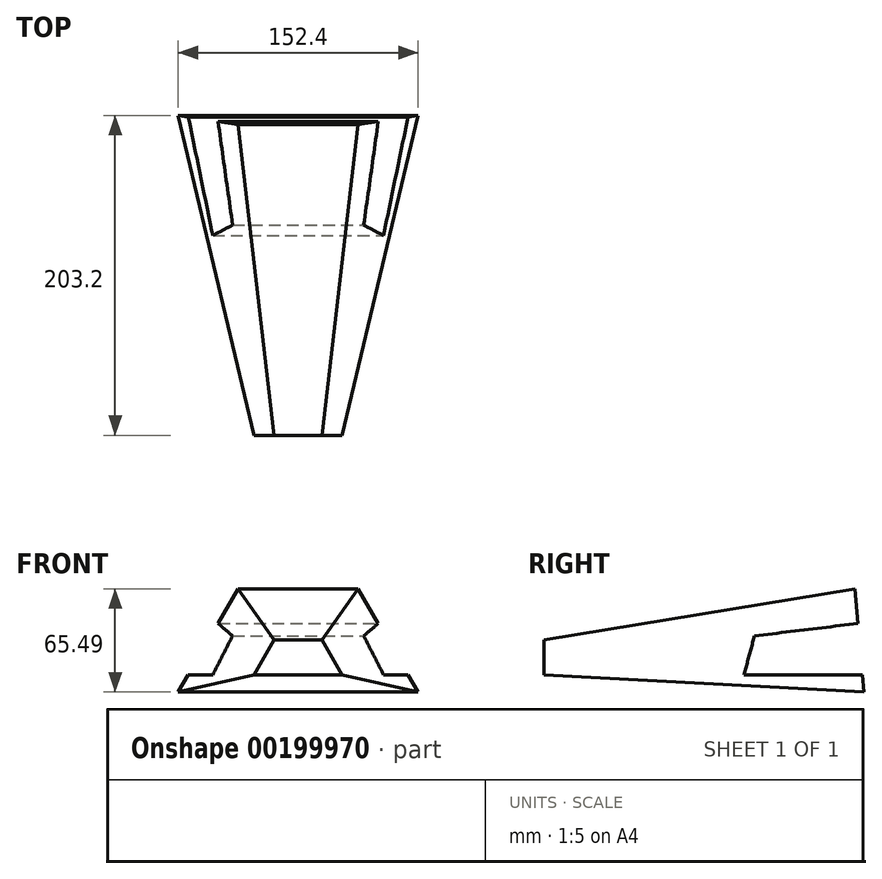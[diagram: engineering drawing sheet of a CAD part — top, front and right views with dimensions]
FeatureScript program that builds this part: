
annotation { "Feature Type Name" : "Feature", "Feature Type Description" : "" }
export const myFeature = defineFeature(function(context is Context, id is Id, definition is map)
    precondition{}
    {
        {
            var Q0;
            Q0=qCreatedBy(makeId("Front.planeOp"),FACE);
            var sketch = newSketch(context, id + "F0", { "sketchPlane" : qUnion([Q0])});
            skLineSegment(sketch, "E0.bottom", {"start": v(76.2, -33) * mm, "end": v(-76.2, -33) * mm});
            skLineSegment(sketch, "E0.top", {"start": v(38.1, 33) * mm, "end": v(-38.1, 33) * mm});
            skPoint(sketch, "E0.middle", {"position": v(0, 0) * mm});
            skLineSegment(sketch, "E1", {"start": v(-76.2, -33) * mm, "end": v(-38.1, 33) * mm});
            skLineSegment(sketch, "E2", {"start": v(0, 78.08) * mm, "end": v(0, -75.73) * mm, "construction": true});
            skLineSegment(sketch, "E3.MirrorCS", {"start": v(76.2, -33) * mm, "end": v(38.1, 33) * mm});
            skPoint(sketch, "E0.right.end.orphan", {"position": v(-76.2, 33) * mm});
            skPoint(sketch, "E0.left.end.orphan", {"position": v(76.2, 33) * mm});
            skSolve(sketch);
        }
        {
            var Q0;
            Q0=qCreatedBy(makeId("Front.planeOp"),FACE);
            cPlane(context, id + "F1", {"entities" : qUnion([Q0]), "cplaneType" : CPlaneType.OFFSET, "offset" : 203.2 * mm, "width" : 152.4 * mm, "height" : 152.4 * mm});
        }
        {
            var Q0;
            Q0=qCreatedBy(id+"F1.planeOp",FACE);
            var sketch = newSketch(context, id + "F2", { "sketchPlane" : qUnion([Q0])});
            skPoint(sketch, "E4.first.point", {"position": v(0, 0) * mm});
            skPoint(sketch, "E4.second.point", {"position": v(0, -22) * mm});
            skLineSegment(sketch, "E5", {"start": v(-27.94, -22) * mm, "end": v(-15.24, 0) * mm});
            skLineSegment(sketch, "E6", {"start": v(-15.24, 0) * mm, "end": v(15.24, 0) * mm});
            skLineSegment(sketch, "E7.MirrorCS", {"start": v(27.94, -22) * mm, "end": v(15.24, 0) * mm});
            skLineSegment(sketch, "E8", {"start": v(-27.94, -22) * mm, "end": v(27.94, -22) * mm});
            skSolve(sketch);
        }
        {
            var Q0;
            Q0=qCreatedBy(makeId("Front.planeOp"),FACE);
            var sketch = newSketch(context, id + "F3", { "sketchPlane" : qUnion([Q0])});
            skPoint(sketch, "E9.2", {"position": v(0, 0) * mm});
            skLineSegment(sketch, "E9.4", {"start": v(0, 78.08) * mm, "end": v(0, -75.73) * mm, "construction": true});
            skPoint(sketch, "E9.6", {"position": v(-76.2, 33) * mm});
            skPoint(sketch, "E9.7", {"position": v(76.2, 33) * mm});
            skLineSegment(sketch, "E10", {"start": v(57.15, 11) * mm, "end": v(-57.15, 11) * mm});
            skLineSegment(sketch, "E11", {"start": v(-57.15, 11) * mm, "end": v(-76.2, -22) * mm});
            skLineSegment(sketch, "E12", {"start": v(-76.2, -22) * mm, "end": v(76.2, -22) * mm});
            skLineSegment(sketch, "E13", {"start": v(76.2, -22) * mm, "end": v(57.15, 11) * mm});
            skPoint(sketch, "E14.orphan", {"position": v(38.1, 33) * mm});
            skPoint(sketch, "E15.orphan", {"position": v(-76.2, -33) * mm});
            skPoint(sketch, "E9.0.start.orphan", {"position": v(76.2, -33) * mm});
            skPoint(sketch, "E9.1.end.orphan", {"position": v(-38.1, 33) * mm});
            skSolve(sketch);
        }
        {
            var Q0;
            Q0=sQuery(id+"F0.wireOp",EDGE,"E0.bottom");
            cPlane(context, id + "F4", {"entities" : qUnion([Q0]), "cplaneType" : CPlaneType.LINE_ANGLE, "offset" : 25.4 * mm, "angle" : 175 * degree, "width" : 152.4 * mm, "height" : 152.4 * mm});
        }
        {
            var Q0;
            Q0=qCreatedBy(id+"F4.planeOp",FACE);
            var sketch = newSketch(context, id + "F5", { "sketchPlane" : qUnion([Q0])});
            skLineSegment(sketch, "E16.0", {"start": v(-76.2, -32.87) * mm, "end": v(76.2, -32.87) * mm});
            skLineSegment(sketch, "E16.1", {"start": v(-38.1, 32.87) * mm, "end": v(38.1, 32.87) * mm});
            skPoint(sketch, "E16.2", {"position": v(0, 0) * mm});
            skLineSegment(sketch, "E16.3", {"start": v(76.2, -32.87) * mm, "end": v(38.1, 32.87) * mm});
            skLineSegment(sketch, "E16.4", {"start": v(0, 77.78) * mm, "end": v(0, -75.44) * mm, "construction": true});
            skLineSegment(sketch, "E16.5", {"start": v(-76.2, -32.87) * mm, "end": v(-38.1, 32.87) * mm});
            skPoint(sketch, "E16.6", {"position": v(76.2, 32.87) * mm});
            skPoint(sketch, "E16.7", {"position": v(-76.2, 32.87) * mm});
            skSolve(sketch);
        }
        {
            var Q0;
            Q0=makeQuery(id+"F5.imprint","IMPRINT",FACE,{"disambiguationData":[TD([[makeQuery(id+"F5.imprint","IMPRINT",EDGE,{"derivedFrom":sQuery(id+"F5.wireOp",EDGE,"E16.0")}),1.0]])]});
            var Q1;
            Q1=makeQuery(id+"F2.imprint","IMPRINT",FACE,{"disambiguationData":[TD([[makeQuery(id+"F2.imprint","IMPRINT",EDGE,{"derivedFrom":sQuery(id+"F2.wireOp",EDGE,"E5")}),-1.0]])]});
            loft(context, id + "F6", {"sheetProfilesArray" : [{ "sheetProfileEntities" : qUnion([Q0]) }, { "sheetProfileEntities" : qUnion([Q1]) }]});
        }
        {
            var Q0;
            Q0=qCreatedBy(makeId("Front.planeOp"),FACE);
            cPlane(context, id + "F7", {"entities" : qUnion([Q0]), "cplaneType" : CPlaneType.OFFSET, "offset" : 76.2 * mm, "width" : 152.4 * mm, "height" : 152.4 * mm});
        }
        {
            var Q0;
            Q0=qCreatedBy(id+"F7.planeOp",FACE);
            var sketch = newSketch(context, id + "F8", { "sketchPlane" : qUnion([Q0])});
            skLineSegment(sketch, "E17.0", {"start": v(57.15, 11) * mm, "end": v(-57.15, 11) * mm, "construction": true});
            skLineSegment(sketch, "E17.1", {"start": v(76.2, -22) * mm, "end": v(57.15, 11) * mm, "construction": true});
            skLineSegment(sketch, "E17.2", {"start": v(-76.2, -22) * mm, "end": v(76.2, -22) * mm, "construction": true});
            skLineSegment(sketch, "E17.3", {"start": v(-57.15, 11) * mm, "end": v(-76.2, -22) * mm, "construction": true});
            skSolve(sketch);
        }
        {
            var Q0;
            Q0=qCreatedBy(id+"F7.planeOp",FACE);
            var Q1;
            Q1=sQuery(id+"F8.wireOp",EDGE,"E17.2");
            cPlane(context, id + "F9", {"entities" : qUnion([Q0, Q1]), "cplaneType" : CPlaneType.LINE_ANGLE, "offset" : 25.4 * mm, "angle" : 165 * degree, "width" : 152.4 * mm, "height" : 152.4 * mm});
        }
        {
            var Q0;
            Q0=qCreatedBy(id+"F9.planeOp",FACE);
            var sketch = newSketch(context, id + "F10", { "sketchPlane" : qUnion([Q0])});
            skLineSegment(sketch, "E18.1", {"start": v(76.2, -40.97) * mm, "end": v(60.96, -15.47) * mm});
            skLineSegment(sketch, "E18.2", {"start": v(-76.2, -40.97) * mm, "end": v(76.2, -40.97) * mm});
            skLineSegment(sketch, "E18.3", {"start": v(-60.96, -15.47) * mm, "end": v(-76.2, -40.97) * mm});
            skLineSegment(sketch, "E19", {"start": v(-60.96, -15.47) * mm, "end": v(60.96, -15.47) * mm});
            skPoint(sketch, "E18.0.end.orphan", {"position": v(-57.15, -9.1) * mm});
            skPoint(sketch, "E18.0.start.orphan", {"position": v(57.15, -9.1) * mm});
            skSolve(sketch);
        }
        {
            var Q1;
            Q1 = qSketchRegion(id + "F10", true);
            var Q2;
            Q2 = qSketchRegion(id + "F3", true);
            loft(context, id + "F11", {"operationType" : NewBodyOperationType.REMOVE, "sheetProfilesArray" : [{ "sheetProfileEntities" : qUnion([Q1]) }, { "sheetProfileEntities" : qUnion([Q2]) }]});
        }
    });
